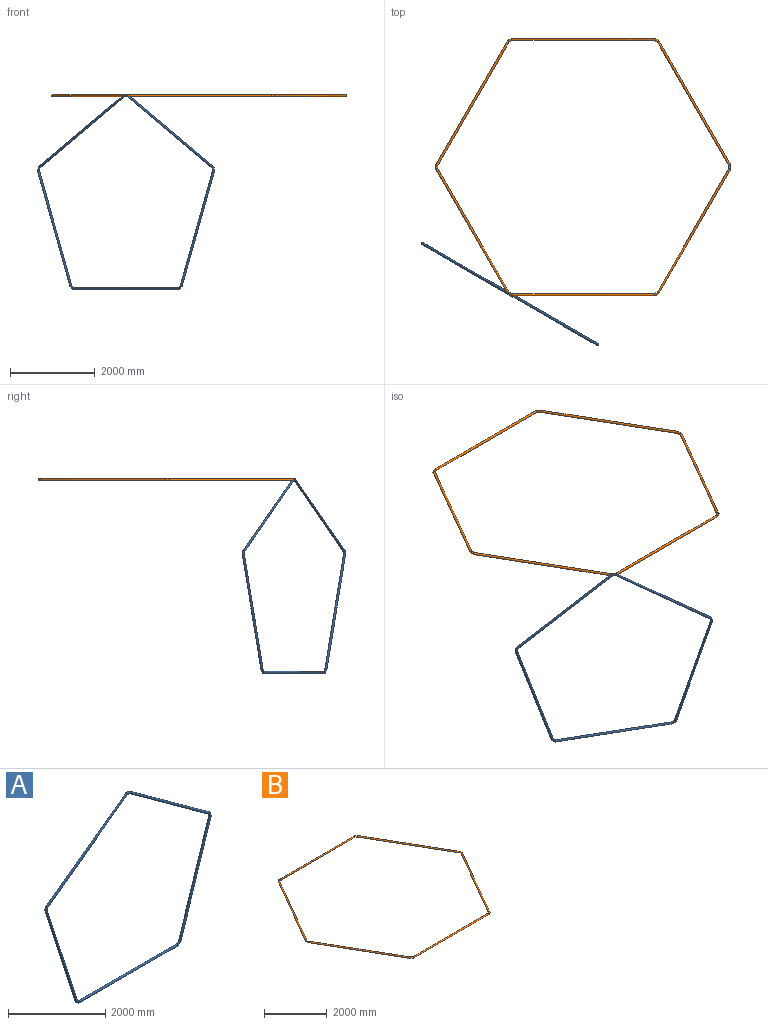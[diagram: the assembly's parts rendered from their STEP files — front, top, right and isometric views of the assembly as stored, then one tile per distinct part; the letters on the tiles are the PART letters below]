
ASSEMBLY  parts=2 mates=1
PART A: 10 faces, bbox 4815.9x50x4580.2 mm
  f0: cylinder r=25mm len=2876.4mm, axis (1,0,0), area 449270.9mm2, adj f1,f2
  f1: cylinder r=25mm len=110.29mm, axis (0.81,0,-0.59), area 13156.1mm2, adj f0,f3
  f2: cylinder r=25mm len=110.3mm, axis (0.81,0,0.59), area 13156.1mm2, adj f0,f4
  f3: cylinder r=25mm len=2751.07mm, axis (0.31,0,-0.95), area 449270.9mm2, adj f1,f5
  f4: cylinder r=25mm len=2751.07mm, axis (0.31,0,0.95), area 449270.9mm2, adj f2,f6
  f5: cylinder r=25mm len=110.56mm, axis (-0.31,0,-0.95), area 13156.1mm2, adj f3,f7
  f6: cylinder r=25mm len=110.56mm, axis (-0.31,0,0.95), area 13156.1mm2, adj f4,f8
  f7: cylinder r=25mm len=2356.45mm, axis (-0.81,0,-0.59), area 449270.9mm2, adj f5,f9
  f8: cylinder r=25mm len=2356.45mm, axis (-0.81,0,0.59), area 449270.9mm2, adj f6,f9
  f9: cylinder r=25mm len=100.01mm, axis (-1,0,0), area 13156.1mm2, adj f7,f8
PART B: 12 faces, bbox 6942.3x6062.2x50 mm
  f0: cylinder r=25mm len=2956.1mm, axis (0.5,0.87,0), area 529536.3mm2, adj f1,f2
  f1: cylinder r=25mm len=100.01mm, axis (0,1,0), area 13603.5mm2, adj f0,f3
  f2: cylinder r=25mm len=111.61mm, axis (0.87,0.5,0), area 13603.5mm2, adj f0,f4
  f3: cylinder r=25mm len=2956.1mm, axis (-0.5,0.87,0), area 529536.3mm2, adj f1,f5
  f4: cylinder r=25mm len=3384.53mm, axis (1,0,0), area 529536.3mm2, adj f2,f6
  f5: cylinder r=25mm len=111.61mm, axis (-0.87,0.5,0), area 13603.5mm2, adj f3,f7
  f6: cylinder r=25mm len=111.61mm, axis (0.87,-0.5,0), area 13603.5mm2, adj f4,f8
  f7: cylinder r=25mm len=3384.54mm, axis (-1,0,0), area 529536.3mm2, adj f5,f9
  f8: cylinder r=25mm len=2956.1mm, axis (0.5,-0.87,0), area 529536.3mm2, adj f6,f10
  f9: cylinder r=25mm len=111.61mm, axis (-0.87,-0.5,0), area 13603.5mm2, adj f7,f11
  f10: cylinder r=25mm len=100.01mm, axis (0,-1,0), area 13603.5mm2, adj f8,f11
  f11: cylinder r=25mm len=2956.1mm, axis (-0.5,-0.87,0), area 529536.3mm2, adj f9,f10
PLACE A rot(axis=(0,0,-1),30deg) t=(-1710.57,-2962.79,-2465.63)mm
PLACE B at identity
MATE revolute A.f9 <-> B.f6  axis (-0.87,0.5,0) through (-1723.07,-2984.44,25)mm
